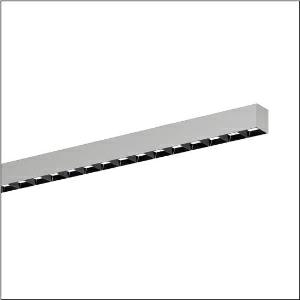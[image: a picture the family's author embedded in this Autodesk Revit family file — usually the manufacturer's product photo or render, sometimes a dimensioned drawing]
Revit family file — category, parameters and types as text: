
# Revit family: silica_r__21_51mx22tctas_2eab
name_source: partatom
category: Lighting Fixtures
units: mm (PartAtom-declared; Revit-internal decimal feet)

## family parameters
Cut with Voids When Loaded = No
Host = Face
Light Source = No
Part Type = Normal
Room Calculation Point = No
Round Connector Dimension = Use Diameter
Shared = No

## types (1)
- --- (1 x LED, 9300 lm, 80.4 W, 6500K)
    Apparent Load = 80 VA
    CIE Flux Codes = 84 100 100 100 100
    Color Rendering = 80
    Color Temperature = 6500K
    Default Elevation = 1800 mm
    Description = Silica® 21, office luminaire, primary light control with darklight reflector, of PMMA, black, CAT 2 (L<= 3000cd/m²), light emission: direct distribution, primary light characteristic: symmetric, installation type: surface-mounted, LED, rated luminous flux: 9.300lm, luminous efficacy: 110lm/W, light colour: 8tw, colour temperature: 2700..6500K, control gear: ECG DALI, with terminal, 3+2-pole, max. 2.5mm², mains connection: 220..240V, AC, 50/60Hz, rated input power: 84.5W, luminaire housing, of aluminium, metallic grey (RAL 9006), length: 3.004mm, width: 53mm, height: 53mm, protection rating (complete): IP20, insulation class (complete): insulation class I (protective earthing), certification: CE, permissible operating ambient temperature: 0..+35°C, standard: EN 50419, packaging unit: 1 piece
    Height = 0 mm  [stored 0 ft]
    Lamp = 1 x LED
    Lamp Light Flux = 9300 lm
    Lamp Power = 80.4 W
    Lamp count = 1
    Length = 3004 mm
    Luminous efficacy = 116 lm/W
    Manufacturer = Siteco
    ModVariant = No
    Model = 51MX22TCTAS
    Mounting Place = Ceiling
    Mounting Type = Recessed
    Number of Poles = 1
    OnlyDefault = Yes
    Power Factor = 1
    Product Name = Silica® 21
    Product group = office luminaire | ceiling recessed
    ProductGroupID = 401
    Protection Class = Protection class I
    Protection Degree = IP 20
    RLX_Detail_Level = 1
    RLX_Emergency_Light_Flux = 0 lm
    RLX_Emergency_Type = 0
    RLX_Emergency_Type_DB = No
    RlxData = <blob elided: 59277 chars, md5=d64a7e2a>
    Socket = socket
    Standby Power = 0 W
    System Light Flux = 9300 lm
    System Power = 80 W
    Type Comments = individual setting
    Type Image = l_1297764.jpg
    URL = http://relux.com
    VarID = @adj_071437
    Voltage = 0 V
    Weight = 0.00 kg
    Width = 53 mm

note: [stored X ft] marks values corroborated as IEEE doubles in the binary element streams (Revit-internal decimal feet)

## geometry (parser evidence)
native form markers: Blend x4, Sweep x11
no freeform markers — native parametric forms only
